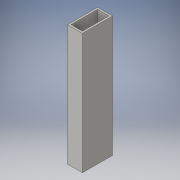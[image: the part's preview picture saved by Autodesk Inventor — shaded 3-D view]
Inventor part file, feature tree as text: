
AUTODESK INVENTOR PART (.ipt)
format: ipt  version: 2016 (Build 200138000, 138)  size: 108,032 bytes
history: native  units: in
note: dims shown in document units (in); Inventor stores cm internally (conversion verified against a paired STEP export)
features: extrude x1, sketch x1
ambient origin geometry x8: Origin, YZ Plane, XZ Plane, XY Plane, X Axis, Y Axis, Z Axis, Center Point
bodies: Solid1 (feature_tree)
feature tree (2):
  extrude  "Extrusion1"  Depth=2.0in
  sketch  "Sketch1"  dims[d0=1.0in d1=2.0in d2=0.125in d3=8.0in d4=0.0in]
